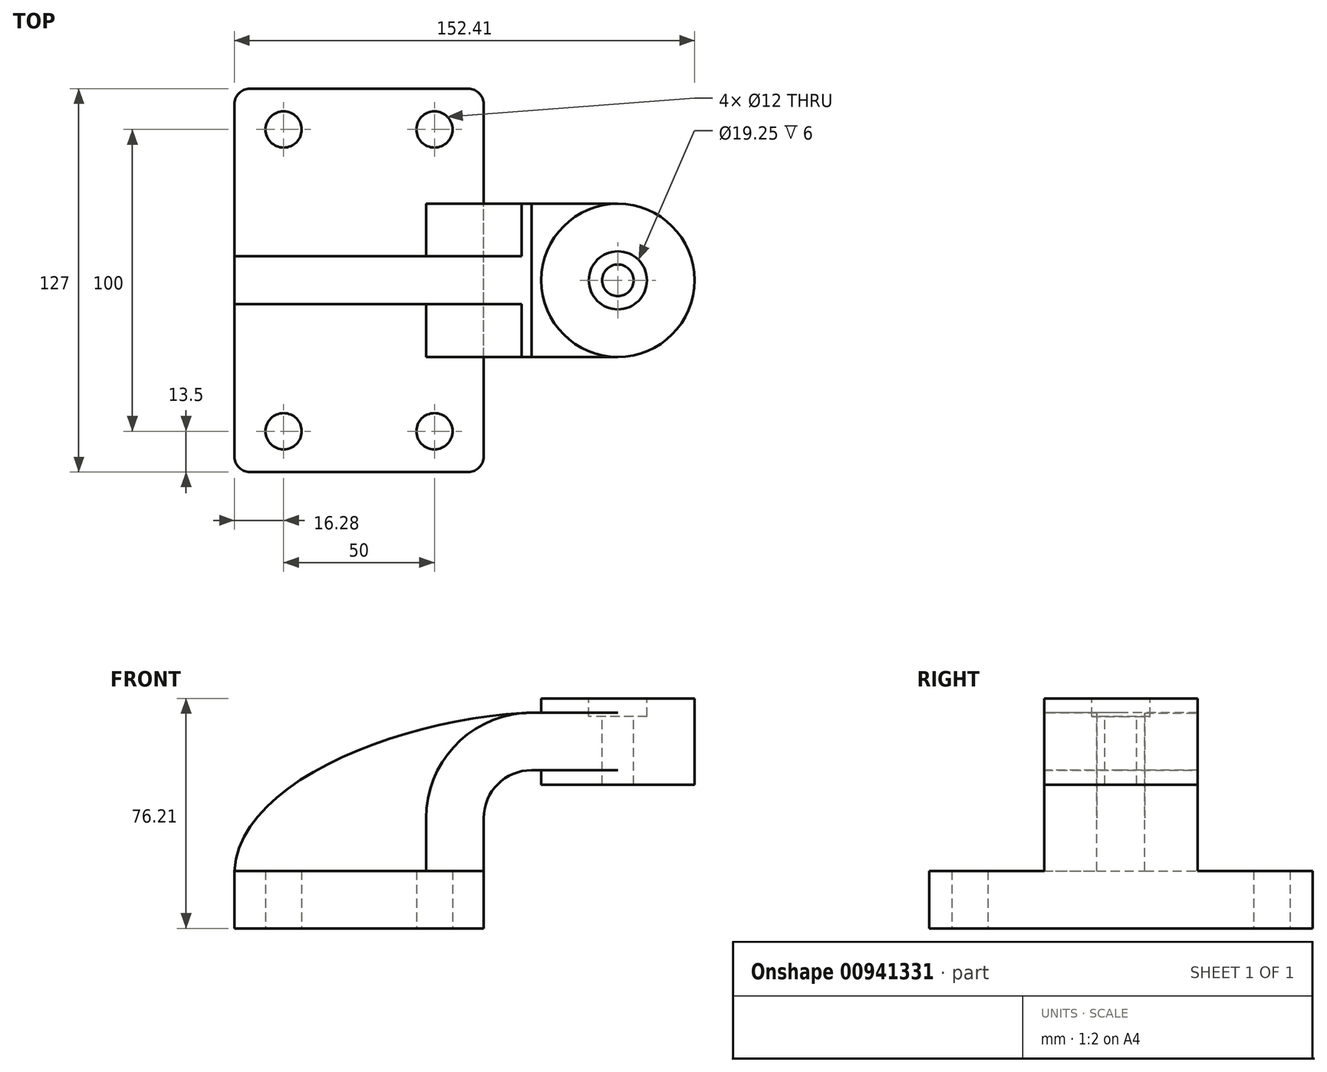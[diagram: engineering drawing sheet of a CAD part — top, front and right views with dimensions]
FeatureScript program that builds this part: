
annotation { "Feature Type Name" : "Feature", "Feature Type Description" : "" }
export const myFeature = defineFeature(function(context is Context, id is Id, definition is map)
    precondition{}
    {
        {
            var Q0;
            Q0=qCreatedBy(makeId("Front.planeOp"),FACE);
            var sketch = newSketch(context, id + "F0", { "sketchPlane" : qUnion([Q0])});
            skLineSegment(sketch, "E0.rect.bottom", {"start": v(-41.28, 9.52) * mm, "end": v(41.28, 9.52) * mm});
            skLineSegment(sketch, "E0.rect.top", {"start": v(-41.28, -9.52) * mm, "end": v(41.28, -9.52) * mm});
            skLineSegment(sketch, "E0.rect.left", {"start": v(-41.28, 9.52) * mm, "end": v(-41.28, -9.52) * mm});
            skLineSegment(sketch, "E0.rect.right", {"start": v(41.28, 9.52) * mm, "end": v(41.28, -9.52) * mm});
            skPoint(sketch, "E0.rect.middle", {"position": v(0, 0) * mm});
            skLineSegment(sketch, "E1", {"start": v(41.28, 9.52) * mm, "end": v(41.28, 27) * mm});
            skArc(sketch, "E2", {"start": v(41.28, 27) * mm, "mid": v(45.92, 38.23) * mm, "end": v(57.15, 42.88) * mm});
            skLineSegment(sketch, "E3", {"start": v(57.15, 42.88) * mm, "end": v(85.72, 42.88) * mm});
            skLineSegment(sketch, "E4.rect.bottom", {"start": v(60.32, 38.1) * mm, "end": v(111.12, 38.1) * mm});
            skLineSegment(sketch, "E4.rect.top", {"start": v(60.32, 66.68) * mm, "end": v(111.12, 66.68) * mm});
            skLineSegment(sketch, "E4.rect.left", {"start": v(60.32, 38.1) * mm, "end": v(60.32, 66.68) * mm});
            skLineSegment(sketch, "E4.rect.right", {"start": v(111.13, 38.1) * mm, "end": v(111.12, 66.68) * mm});
            skPoint(sketch, "E4.rect.middle", {"position": v(85.72, 52.39) * mm});
            skLineSegment(sketch, "E5.0", {"start": v(57.15, 61.93) * mm, "end": v(85.72, 61.93) * mm});
            skArc(sketch, "E5.1", {"start": v(22.23, 27) * mm, "mid": v(32.45, 51.7) * mm, "end": v(57.15, 61.93) * mm});
            skLineSegment(sketch, "E5.2", {"start": v(22.23, 9.52) * mm, "end": v(22.23, 27) * mm});
            skLineSegment(sketch, "E6", {"start": v(85.72, 38.1) * mm, "end": v(85.72, 66.68) * mm});
            skFitSpline(sketch, "E7", {"points": [v(-41.28, 9.53) * mm, v(57.15, 61.93) * mm], "startDerivative": vector(5.2, 92.34) * mm, "endDerivative": vector(120.92, 4.22) * mm});
            skSolve(sketch);
        }
        {
            var Q0;
            Q0=makeQuery(id+"F0.imprint","IMPRINT",FACE,{"disambiguationData":[TD([[makeQuery(id+"F0.imprint","IMPRINT",EDGE,{"derivedFrom":sQuery(id+"F0.wireOp",EDGE,"E0.rect.top")}),1.0]])]});
            extrude(context, id + "F1", {"entities" : qUnion([Q0]), "endBound" : BoundingType.SYMMETRIC, "depth" : 127 * mm});
        }
        {
            var Q0;
            {var subQ9=sQuery(id+"F0.wireOp",EDGE,"E1");Q0=makeQuery(id+"F0.imprint","IMPRINT",FACE,{"disambiguationData":[TD([[makeQuery(id+"F0.imprint","IMPRINT",EDGE,{"derivedFrom":subQ9}),1.0]])]});}
            var Q1;
            {var subQ0=sQuery(id+"F0.wireOp",EDGE,"E6");var subQ1=sQuery(id+"F0.wireOp",EDGE,"E3");var subQ2=makeQuery(id+"F0.imprint","INTERSECT",VERTEX,{"derivedFrom":[subQ1,subQ0]});Q1=makeQuery(id+"F0.imprint","IMPRINT",FACE,{"disambiguationData":[TD([[makeQuery(id+"F0.imprint","IMPRINT",EDGE,{"disambiguationData":[TD([[subQ2,1.0]])],"derivedFrom":subQ1}),1.0]])]});}
            extrude(context, id + "F2", {"entities" : qUnion([Q0, Q1]), "operationType" : NewBodyOperationType.ADD, "endBound" : BoundingType.SYMMETRIC, "depth" : 50.8 * mm});
        }
        {
            var Q0;
            {var subQ3=sQuery(id+"F0.wireOp",EDGE,"E5.2");Q0=makeQuery(id+"F0.imprint","IMPRINT",FACE,{"disambiguationData":[TD([[makeQuery(id+"F0.imprint","IMPRINT",EDGE,{"derivedFrom":subQ3}),1.0]])]});}
            extrude(context, id + "F3", {"entities" : qUnion([Q0]), "operationType" : NewBodyOperationType.ADD, "endBound" : BoundingType.SYMMETRIC, "depth" : 15.88 * mm});
        }
        {
            var Q0;
            {var subQ5=sQuery(id+"F0.wireOp",EDGE,"E4.rect.right");Q0=makeQuery(id+"F0.imprint","IMPRINT",FACE,{"disambiguationData":[TD([[makeQuery(id+"F0.imprint","IMPRINT",EDGE,{"derivedFrom":subQ5}),1.0]])]});}
            var Q1;
            Q1=sQuery(id+"F0.wireOp",EDGE,"E6");
            revolve(context, id + "F4", {"operationType" : NewBodyOperationType.ADD, "entities" : qUnion([Q0]), "axis" : qUnion([Q1]), "revolveType" : RevolveType.FULL});
        }
        {
            var Q0;
            Q0=makeQuery(id+"F1.opExtrude","CAP_EDGE",EDGE,{"disambiguationData":[OSD([sQuery(id+"F0.wireOp",EDGE,"E0.rect.right")])],"isStart":false});
            var Q1;
            Q1=makeQuery(id+"F1.opExtrude","CAP_EDGE",EDGE,{"disambiguationData":[OSD([sQuery(id+"F0.wireOp",EDGE,"E0.rect.left")])],"isStart":false});
            var Q2;
            Q2=makeQuery(id+"F1.opExtrude","CAP_EDGE",EDGE,{"disambiguationData":[OSD([sQuery(id+"F0.wireOp",EDGE,"E0.rect.right")])],"isStart":true});
            var Q3;
            Q3=makeQuery(id+"F1.opExtrude","CAP_EDGE",EDGE,{"disambiguationData":[OSD([sQuery(id+"F0.wireOp",EDGE,"E0.rect.left")])],"isStart":true});
            fillet(context, id + "F5", {"entities" : qUnion([Q0, Q1, Q2, Q3]), "radius" : 5.08 * mm, "tangentPropagation" : true, "allowEdgeOverflow" : false});
        }
        {
            var Q0;
            Q0=makeQuery(id+"F4.opRevolve","SWEPT_FACE",FACE,{"disambiguationData":[OSD([sQuery(id+"F0.wireOp",EDGE,"E4.rect.top")])]});
            var sketch = newSketch(context, id + "F6", { "sketchPlane" : qUnion([Q0])});
            skPoint(sketch, "E8", {"position": v(85.72, 0) * mm});
            skSolve(sketch);
        }
        {
            var Q0;
            Q0=sQuery(id+"F6.wireOp",VERTEX,"E8");
            var Q1;
            Q1=makeQuery(id+"F1.opExtrude","SWEPT_BODY",BODY,{"disambiguationData":[OSD([sQuery(id+"F0.wireOp",EDGE,"E0.rect.bottom"),sQuery(id+"F0.wireOp",EDGE,"E0.rect.top"),sQuery(id+"F0.wireOp",EDGE,"E0.rect.left"),sQuery(id+"F0.wireOp",EDGE,"E0.rect.right")])]});
            hole(context, id + "F7", {"style" : HoleStyle.C_BORE, "endStyle" : HoleEndStyle.THROUGH, "holeDiameter" : 10.5 * mm, "cBoreDiameter" : 19.25 * mm, "cBoreDepth" : 6 * mm, "majorDiameter" : 12 * mm, "isTappedThrough" : true, "tappedDepth" : 7.5 * mm, "tapClearance" : 3, "locations" : qUnion([Q0]), "scope" : qUnion([Q1])});
        }
        {
            var Q0;
            Q0=makeQuery(id+"F1.opExtrude","SWEPT_FACE",FACE,{"disambiguationData":[OSD([sQuery(id+"F0.wireOp",EDGE,"E0.rect.top")])]});
            var sketch = newSketch(context, id + "F8", { "sketchPlane" : qUnion([Q0])});
            skLineSegment(sketch, "E9.bottom", {"start": v(25, 50) * mm, "end": v(-25, 50) * mm});
            skLineSegment(sketch, "E9.top", {"start": v(25, -50) * mm, "end": v(-25, -50) * mm});
            skLineSegment(sketch, "E9.left", {"start": v(25, 50) * mm, "end": v(25, -50) * mm});
            skLineSegment(sketch, "E9.right", {"start": v(-25, 50) * mm, "end": v(-25, -50) * mm});
            skPoint(sketch, "E9.middle", {"position": v(0, 0) * mm});
            skSolve(sketch);
        }
        {
            var Q0;
            Q0=sQuery(id+"F8.wireOp",VERTEX,"E9.bottom.end");
            var Q1;
            Q1=sQuery(id+"F8.wireOp",VERTEX,"E9.bottom.start");
            var Q2;
            Q2=sQuery(id+"F8.wireOp",VERTEX,"E9.top.start");
            var Q3;
            Q3=sQuery(id+"F8.wireOp",VERTEX,"E9.top.end");
            var Q4;
            Q4=makeQuery(id+"F1.opExtrude","SWEPT_BODY",BODY,{"disambiguationData":[OSD([sQuery(id+"F0.wireOp",EDGE,"E0.rect.bottom"),sQuery(id+"F0.wireOp",EDGE,"E0.rect.top"),sQuery(id+"F0.wireOp",EDGE,"E0.rect.left"),sQuery(id+"F0.wireOp",EDGE,"E0.rect.right")])]});
            hole(context, id + "F9", {"style" : HoleStyle.SIMPLE, "endStyle" : HoleEndStyle.THROUGH, "holeDiameter" : 12 * mm, "majorDiameter" : 5 * mm, "isTappedThrough" : true, "tappedDepth" : 7.5 * mm, "tapClearance" : 3, "locations" : qUnion([Q0, Q1, Q2, Q3]), "scope" : qUnion([Q4])});
        }
    });
